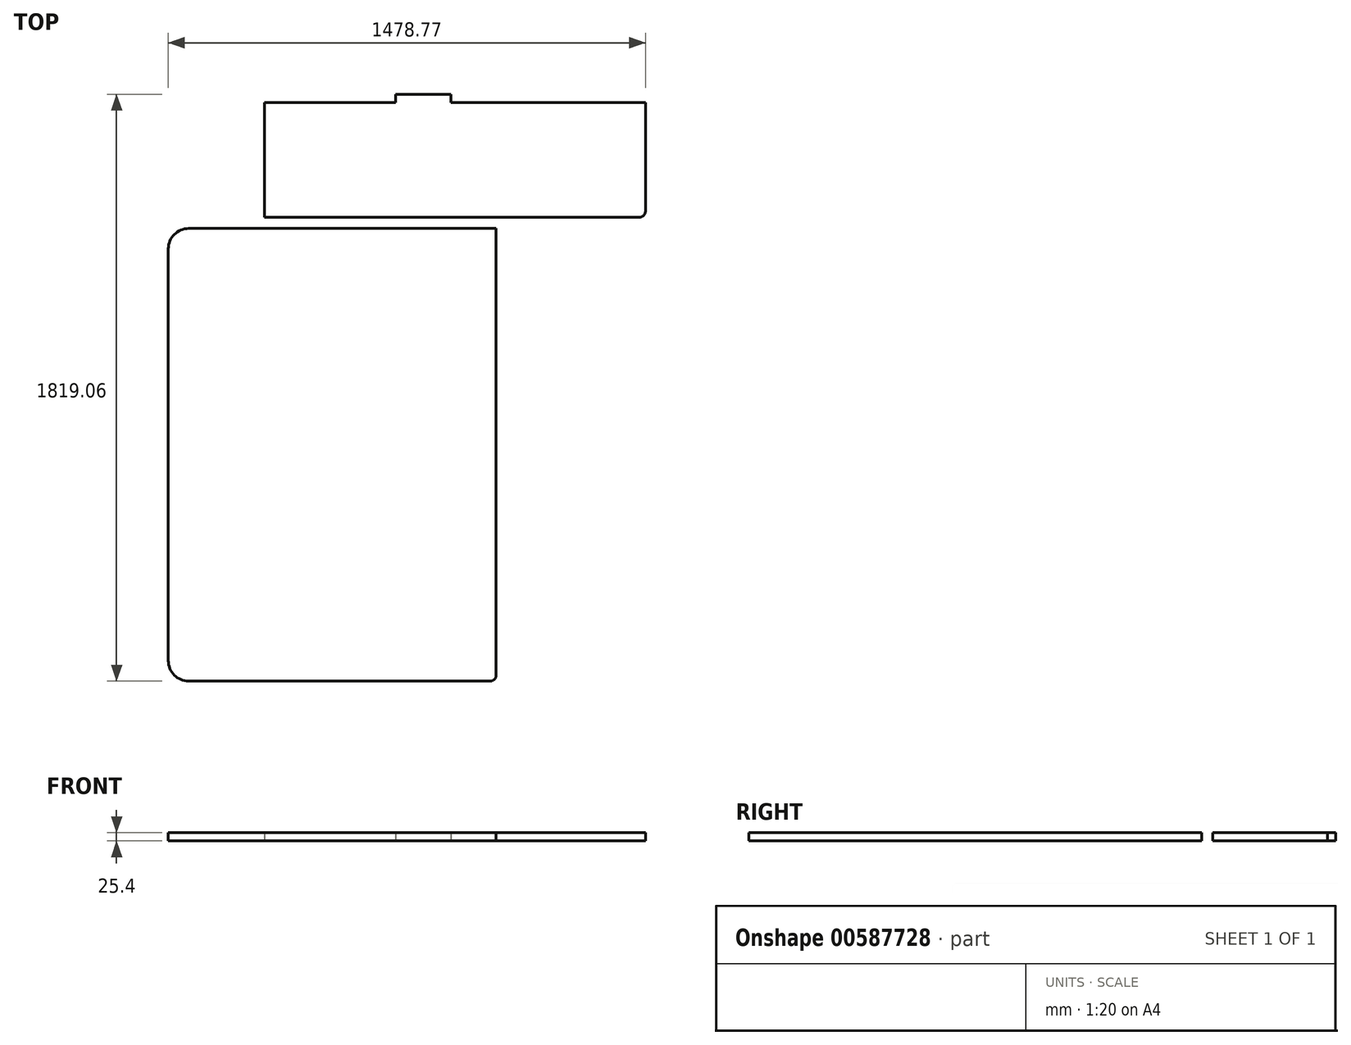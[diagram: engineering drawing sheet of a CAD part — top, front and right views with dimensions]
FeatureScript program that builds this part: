
annotation { "Feature Type Name" : "Feature", "Feature Type Description" : "" }
export const myFeature = defineFeature(function(context is Context, id is Id, definition is map)
    precondition{}
    {
        {
            var Q0;
            Q0=qCreatedBy(makeId("Top.planeOp"),FACE);
            var sketch = newSketch(context, id + "F0", { "sketchPlane" : qUnion([Q0])});
            skLineSegment(sketch, "E0", {"start": v(-694.09, 357.05) * mm, "end": v(-694.09, -934.42) * mm});
            skLineSegment(sketch, "E1", {"start": v(-630.59, -997.92) * mm, "end": v(302.86, -997.92) * mm});
            skLineSegment(sketch, "E2", {"start": v(321.91, -978.87) * mm, "end": v(321.91, 405.43) * mm});
            skPoint(sketch, "E3.visualSharp", {"position": v(791.81, 405.43) * mm});
            skPoint(sketch, "E4.visualSharp", {"position": v(321.91, -997.92) * mm});
            skArc(sketch, "E4.filletArc", {"start": v(302.86, -997.92) * mm, "mid": v(316.33, -992.34) * mm, "end": v(321.91, -978.87) * mm});
            skPoint(sketch, "E5.visualSharp", {"position": v(-694.09, -997.92) * mm});
            skArc(sketch, "E5.filletArc", {"start": v(-694.09, -934.42) * mm, "mid": v(-675.49, -979.32) * mm, "end": v(-630.59, -997.92) * mm});
            skLineSegment(sketch, "E6.bottom", {"start": v(296.51, -972.52) * mm, "end": v(-351.19, -972.52) * mm, "construction": true});
            skLineSegment(sketch, "E6.left", {"start": v(296.51, -972.52) * mm, "end": v(296.51, 405.43) * mm, "construction": true});
            skLineSegment(sketch, "E6.right", {"start": v(-351.19, -972.52) * mm, "end": v(-351.19, 405.43) * mm, "construction": true});
            skLineSegment(sketch, "E7", {"start": v(-389.29, 405.43) * mm, "end": v(-630.59, 405.43) * mm});
            skLineSegment(sketch, "E8", {"start": v(-694.09, 357.05) * mm, "end": v(-694.09, 341.93) * mm});
            skPoint(sketch, "E9.visualSharp", {"position": v(-694.09, 405.43) * mm});
            skArc(sketch, "E9.filletArc", {"start": v(-630.59, 405.43) * mm, "mid": v(-675.49, 386.84) * mm, "end": v(-694.09, 341.93) * mm});
            skLineSegment(sketch, "E10", {"start": v(321.91, 405.43) * mm, "end": v(-389.29, 405.43) * mm});
            skSolve(sketch);
        }
        {
            var Q0;
            Q0 = qSketchRegion(id + "F0", true);
            extrude(context, id + "F1", {"entities" : qUnion([Q0]), "depth" : 25.4 * mm, "offsetDistance" : 25.4 * mm});
        }
        {
            var Q0;
            Q0=qCreatedBy(makeId("Top.planeOp"),FACE);
            var sketch = newSketch(context, id + "F2", { "sketchPlane" : qUnion([Q0])});
            skLineSegment(sketch, "E11", {"start": v(208.26, 440.14) * mm, "end": v(765.63, 440.14) * mm});
            skLineSegment(sketch, "E12", {"start": v(784.68, 459.2) * mm, "end": v(784.68, 795.74) * mm});
            skLineSegment(sketch, "E13", {"start": v(784.68, 795.74) * mm, "end": v(181.43, 795.74) * mm});
            skLineSegment(sketch, "E14", {"start": v(9.98, 795.74) * mm, "end": v(9.98, 821.14) * mm});
            skLineSegment(sketch, "E15", {"start": v(9.98, 821.14) * mm, "end": v(181.43, 821.14) * mm});
            skLineSegment(sketch, "E16", {"start": v(181.43, 821.14) * mm, "end": v(181.43, 795.74) * mm});
            skArc(sketch, "E17.filletArc", {"start": v(765.63, 440.14) * mm, "mid": v(779.1, 445.72) * mm, "end": v(784.68, 459.2) * mm});
            skLineSegment(sketch, "E18", {"start": v(9.98, 795.74) * mm, "end": v(-396.42, 440.14) * mm, "construction": true});
            skLineSegment(sketch, "E19", {"start": v(9.98, 795.74) * mm, "end": v(-396.42, 795.74) * mm});
            skLineSegment(sketch, "E20", {"start": v(-396.42, 795.74) * mm, "end": v(-396.42, 440.14) * mm});
            skLineSegment(sketch, "E21", {"start": v(208.26, 440.14) * mm, "end": v(-396.42, 440.14) * mm});
            skSolve(sketch);
        }
        {
            var Q0;
            Q0 = qSketchRegion(id + "F2", true);
            extrude(context, id + "F3", {"entities" : qUnion([Q0]), "depth" : 25.4 * mm, "offsetDistance" : 25.4 * mm});
        }
    });
